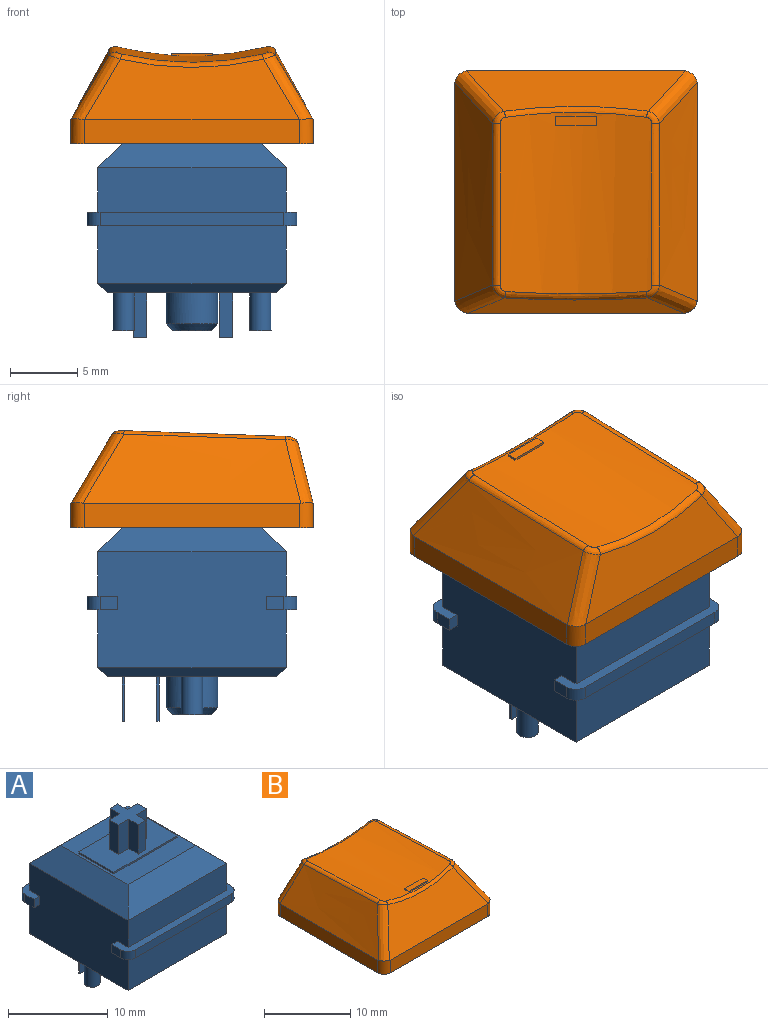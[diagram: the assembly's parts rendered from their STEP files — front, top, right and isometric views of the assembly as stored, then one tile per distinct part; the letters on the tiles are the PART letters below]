
ASSEMBLY  parts=2 mates=1
PART A: 69 faces, bbox 15.6x15.6x18.6 mm
  f0: plane 15.6x2.3mm, normal (0,0,-1), area 14.4mm2, adj f2,f3,f28,f30,f35,f60,f62,f63
  f1: plane 15.6x2.3mm, normal (0,0,-1), area 14.4mm2, adj f28,f30,f33,f34,f36,f59,f61,f64
  f2: plane 1.3x1mm, normal (1,0,0), area 1.3mm2, adj f0,f32,f62,f66
  f3: plane 1.3x1mm, normal (-1,0,0), area 1.3mm2, adj f0,f32,f63,f68
  f4: plane 15.6x2.3mm, normal (0,0,1), area 14.4mm2, adj f28,f30,f31,f33,f34,f36,f61,f64
  f5: plane 14x2.2mm, normal (-0.71,0,0.71), area 36.7mm2, adj f6,f7,f26,f30
  f6: plane 14x2.2mm, normal (0,-0.71,0.71), area 36.7mm2, adj f5,f7,f27,f31
  f7: plane 9.6x9.6mm, normal (0,0,1), area 47.2mm2, adj f5,f6,f8,f9,f10,f11,f26,f27
  f8: plane 5x0.2mm, normal (1,0,0), area 1mm2, adj f7,f9,f11,f12
  f9: plane 9x0.2mm, normal (0,1,0), area 1.8mm2, adj f7,f8,f10,f12
  f10: plane 5x0.2mm, normal (-1,0,0), area 1mm2, adj f7,f9,f11,f12
  f11: plane 9x0.2mm, normal (0,-1,0), area 1.8mm2, adj f7,f8,f10,f12
  f12: plane 9x5mm, normal (0,0,1), area 36.9mm2, adj f8,f9,f10,f11,f13,f14,f15,f16
  f13: plane 3.6x1.35mm, normal (1,0,0), area 4.9mm2, adj f12,f14,f24,f25
  f14: plane 3.6x1.08mm, normal (0,1,0), area 3.9mm2, adj f12,f13,f15,f25
  f15: plane 3.6x1.35mm, normal (-1,0,0), area 4.9mm2, adj f12,f14,f16,f25
  f16: plane 3.6x1.46mm, normal (0,1,0), area 5.3mm2, adj f12,f15,f17,f25
  f17: plane 3.6x1.3mm, normal (-1,0,0), area 4.7mm2, adj f12,f16,f18,f25
  f18: plane 3.6x1.46mm, normal (0,-1,0), area 5.3mm2, adj f12,f17,f19,f25
  f19: plane 3.6x1.35mm, normal (-1,0,0), area 4.9mm2, adj f12,f18,f20,f25
  f20: plane 3.6x1.08mm, normal (0,-1,0), area 3.9mm2, adj f12,f19,f21,f25
  f21: plane 3.6x1.35mm, normal (1,0,0), area 4.9mm2, adj f12,f20,f22,f25
  f22: plane 3.6x1.46mm, normal (0,-1,0), area 5.3mm2, adj f12,f21,f23,f25
  f23: plane 3.6x1.3mm, normal (1,0,0), area 4.7mm2, adj f12,f22,f24,f25
  f24: plane 3.6x1.46mm, normal (0,1,0), area 5.3mm2, adj f12,f13,f23,f25
  f25: plane 4x4mm, normal (0,0,1), area 8.1mm2, adj f13,f14,f15,f16,f17,f18,f19,f20
  f26: plane 14x2.2mm, normal (0,0.71,0.71), area 36.7mm2, adj f5,f7,f27,f29
  f27: plane 14x2.2mm, normal (0.71,0,0.71), area 36.7mm2, adj f6,f7,f26,f28
  f28: plane 14x8.6mm, normal (1,0,0), area 117.4mm2, adj f0,f1,f4,f27,f29,f31,f32,f55
  f29: plane 14x3.3mm, normal (0,1,0), area 46.2mm2, adj f26,f28,f30,f32
  f30: plane 14x8.6mm, normal (-1,0,0), area 117.4mm2, adj f0,f1,f4,f5,f29,f31,f32,f57
  f31: plane 14x3.3mm, normal (0,-1,0), area 46.2mm2, adj f4,f6,f28,f30
  f32: plane 15.6x2.3mm, normal (0,0,1), area 14.4mm2, adj f2,f3,f28,f29,f30,f35,f62,f63
  f33: plane 13.6x1mm, normal (0,-1,0), area 13.6mm2, adj f1,f4,f61,f64
  f34: plane 1.3x1mm, normal (1,0,0), area 1.3mm2, adj f1,f4,f61,f65
  f35: plane 13.6x1mm, normal (0,1,0), area 13.6mm2, adj f0,f32,f62,f63
  f36: plane 1.3x1mm, normal (-1,0,0), area 1.3mm2, adj f1,f4,f64,f67
  f37: plane 2.85x2.85mm, normal (0,0,-1), area 6.4mm2, adj f38
  f38: cone r=1.43mm half-angle=45deg, axis (0,0,1), area 7.4mm2, adj f37,f43
  f39: plane 1x0.2mm, normal (0,0,-1), area 0.2mm2, adj f44,f45,f46,f47
  f40: plane 1x0.2mm, normal (0,0,-1), area 0.2mm2, adj f48,f49,f50,f51
  f41: plane 1.6x1.6mm, normal (0,0,-1), area 2mm2, adj f52
  f42: plane 1.6x1.6mm, normal (0,0,-1), area 2mm2, adj f53
  f43: cylinder r=1.93mm len=3.85mm, axis (0,0,1), area 27.8mm2, adj f38,f54
  f44: plane 3.3x0.2mm, normal (-1,0,0), area 0.7mm2, adj f39,f45,f47,f54
  f45: plane 3.3x1mm, normal (0,1,0), area 3.3mm2, adj f39,f44,f46,f54
  f46: plane 3.3x0.2mm, normal (1,0,0), area 0.7mm2, adj f39,f45,f47,f54
  f47: plane 3.3x1mm, normal (0,-1,0), area 3.3mm2, adj f39,f44,f46,f54
  f48: plane 3.3x0.2mm, normal (-1,0,0), area 0.7mm2, adj f40,f49,f51,f54
  f49: plane 3.3x1mm, normal (0,1,0), area 3.3mm2, adj f40,f48,f50,f54
  f50: plane 3.3x0.2mm, normal (1,0,0), area 0.7mm2, adj f40,f49,f51,f54
  f51: plane 3.3x1mm, normal (0,-1,0), area 3.3mm2, adj f40,f48,f50,f54
  f52: cylinder r=0.8mm len=2.8mm, axis (0,0,1), area 14.1mm2, adj f41,f54
  f53: cylinder r=0.8mm len=2.8mm, axis (0,0,1), area 14.1mm2, adj f42,f54
  f54: plane 12.6x12.6mm, normal (0,0,-1), area 142.7mm2, adj f43,f44,f45,f46,f47,f48,f49,f50
  f55: plane 14x0.7mm, normal (0.71,0,-0.71), area 13.2mm2, adj f28,f54,f56,f58
  f56: plane 14x0.7mm, normal (0,0.71,-0.71), area 13.2mm2, adj f54,f55,f57,f60
  f57: plane 14x0.7mm, normal (-0.71,0,-0.71), area 13.2mm2, adj f30,f54,f56,f58
  f58: plane 14x0.7mm, normal (0,-0.71,-0.71), area 13.2mm2, adj f54,f55,f57,f59
  f59: plane 14x4.3mm, normal (0,-1,0), area 60.2mm2, adj f1,f28,f30,f58
  f60: plane 14x4.3mm, normal (0,1,0), area 60.2mm2, adj f0,f28,f30,f56
  f61: cylinder r=1mm len=1mm, axis (0,0,-1), area 1.6mm2, adj f1,f4,f33,f34
  f62: cylinder r=1mm len=1mm, axis (0,0,1), area 1.6mm2, adj f0,f2,f32,f35
  f63: cylinder r=1mm len=1mm, axis (0,0,-1), area 1.6mm2, adj f0,f3,f32,f35
  f64: cylinder r=1mm len=1mm, axis (0,0,1), area 1.6mm2, adj f1,f4,f33,f36
  f65: plane 1x0.8mm, normal (0,1,0), area 0.8mm2, adj f1,f4,f28,f34
  f66: plane 1x0.8mm, normal (0,-1,0), area 0.8mm2, adj f0,f2,f28,f32
  f67: plane 1x0.8mm, normal (0,1,0), area 0.8mm2, adj f1,f4,f30,f36
  f68: plane 1x0.8mm, normal (0,-1,0), area 0.8mm2, adj f0,f3,f30,f32
PART B: 55 faces, bbox 21.6x21x10.3 mm
  f0: cylinder r=22.9mm len=13.32mm, axis (0,1,-0.04), area 147.4mm2, adj f18,f19,f20,f21,f22,f23,f24,f25
  f1: plane 18x18mm, normal (0,0,-1), area 67.1mm2, adj f2,f3,f4,f5,f10,f12,f14,f16
  f2: plane 16x1.8mm, normal (1,0,0), area 28.8mm2, adj f1,f9,f10,f16
  f3: plane 16x1.8mm, normal (0,1,0), area 28.8mm2, adj f1,f6,f14,f15,f16,f17
  f4: plane 16x1.8mm, normal (-1,0,0), area 28.8mm2, adj f1,f7,f12,f14
  f5: plane 16x1.8mm, normal (0,-1,0), area 28.8mm2, adj f1,f8,f10,f12
  f6: plane 15.96x4.48mm, normal (0,0.97,0.24), area 56.8mm2, adj f3,f15,f17,f20
  f7: bspline ~18x5.51mm, area 80.2mm2, adj f4,f12,f13,f14,f15,f19
  f8: plane 16.27x5.09mm, normal (0,-0.86,0.51), area 74.6mm2, adj f5,f10,f11,f12,f13,f23
  f9: bspline ~18x5.51mm, area 80.2mm2, adj f2,f10,f11,f16,f17,f24
  f10: cylinder r=1mm len=1.89mm, axis (0,0,-1), area 2.9mm2, adj f1,f2,f5,f8,f9,f11
  f11: bspline ~6.77x4.7mm, area 8.7mm2, adj f8,f9,f10,f25
  f12: cylinder r=1mm len=1.89mm, axis (0,0,1), area 2.9mm2, adj f1,f4,f5,f7,f8,f13
  f13: bspline ~6.77x4.7mm, area 8.7mm2, adj f7,f8,f12,f21
  f14: cylinder r=1mm len=1.81mm, axis (0,0,-1), area 2.8mm2, adj f1,f3,f4,f7,f15
  f15: bspline ~8.13x5.44mm, area 7.9mm2, adj f3,f6,f7,f14,f18
  f16: cylinder r=1mm len=1.81mm, axis (0,0,1), area 2.8mm2, adj f1,f2,f3,f9,f17
  f17: bspline ~8.13x5.44mm, area 7.9mm2, adj f3,f6,f9,f16,f22
  f18: bspline ~1.19x1.01mm, area 0.7mm2, adj f0,f15,f19,f20
  f19: bspline ~16.72x0.91mm, area 7.8mm2, adj f0,f7,f18,f21
  f20: bspline ~10.66x0.99mm, area 6.9mm2, adj f0,f6,f18,f22
  f21: bspline ~1.2x1.09mm, area 0.6mm2, adj f0,f13,f19,f23
  f22: bspline ~1.17x1.02mm, area 0.7mm2, adj f0,f17,f20,f24
  f23: bspline ~10.72x0.84mm, area 5.8mm2, adj f0,f8,f21,f25
  f24: bspline ~16.72x0.91mm, area 7.8mm2, adj f0,f9,f22,f25
  f25: bspline ~1.2x1.09mm, area 0.6mm2, adj f0,f11,f23,f24
  f26: plane 16.02x1.56mm, normal (-1,0,0), area 24.6mm2, adj f1,f27,f29,f33
  f27: plane 16x1.68mm, normal (0,-1,0), area 26.8mm2, adj f1,f26,f28,f30,f31,f33
  f28: plane 16.02x1.56mm, normal (1,0,0), area 24.6mm2, adj f1,f27,f29,f31
  f29: plane 16.02x1.54mm, normal (0,1,0), area 24.4mm2, adj f1,f26,f28,f32
  f30: plane 16.19x4.4mm, normal (0,-0.97,-0.24), area 50.7mm2, adj f27,f31,f33,f34
  f31: offset ~20x7.51mm, area 71.4mm2, adj f27,f28,f30,f32,f34
  f32: plane 16.71x5.3mm, normal (0,0.86,-0.51), area 66.9mm2, adj f29,f31,f33,f34
  f33: offset ~20x7.51mm, area 71.4mm2, adj f26,f27,f30,f32,f34
  f34: cylinder r=23.9mm len=12.29mm, axis (0,1,-0.04), area 112.6mm2, adj f30,f31,f32,f33,f46
  f35: plane 4.69x1.5mm, normal (-1,0,0), area 7mm2, adj f36,f44,f45,f49
  f36: plane 4.78x1.5mm, normal (0,-1,0), area 7.1mm2, adj f35,f37,f45,f49
  f37: plane 4.82x1.3mm, normal (-1,0,0), area 6.2mm2, adj f36,f38,f45,f49
  f38: plane 4.82x1.5mm, normal (0,1,0), area 7.2mm2, adj f37,f39,f45,f49
  f39: plane 4.79x1.5mm, normal (-1,0,0), area 7.1mm2, adj f38,f40,f45,f49
  f40: plane 4.79x1.3mm, normal (0,1,0), area 6.2mm2, adj f39,f41,f45,f49
  f41: plane 4.79x1.5mm, normal (1,0,0), area 7.1mm2, adj f40,f42,f45,f49
  f42: plane 4.82x1.5mm, normal (0,1,0), area 7.2mm2, adj f41,f43,f45,f49
  f43: plane 4.82x1.3mm, normal (1,0,0), area 6.2mm2, adj f42,f45,f47,f49
  f44: plane 4.64x1.3mm, normal (0,-1,0), area 6mm2, adj f35,f45,f48,f49
  f45: plane 5.5x5.5mm, normal (0,0,-1), area 14.3mm2, adj f35,f36,f37,f38,f39,f40,f41,f42
  f46: cylinder r=2.75mm len=5.5mm, axis (0,0,-1), area 84mm2, adj f34,f45
  f47: plane 4.78x1.5mm, normal (0,-1,0), area 7.1mm2, adj f43,f45,f48,f49
  f48: plane 4.69x1.5mm, normal (1,0,0), area 7mm2, adj f44,f45,f47,f49
  f49: cylinder r=23.9mm len=4.3mm, axis (0,1,-0.04), area 9.5mm2, adj f35,f36,f37,f38,f39,f40,f41,f42
  f50: plane 0.71x0.18mm, normal (1,0,0), area 0.1mm2, adj f0,f51,f53,f54
  f51: plane 3x0.2mm, normal (0,1,-0.04), area 0.6mm2, adj f0,f50,f52,f54
  f52: plane 0.71x0.18mm, normal (-1,0,0), area 0.1mm2, adj f0,f51,f53,f54
  f53: plane 3x0.2mm, normal (0,-1,0.04), area 0.6mm2, adj f0,f50,f52,f54
  f54: plane 3x0.7mm, normal (0,0.04,1), area 2.1mm2, adj f50,f51,f52,f53
PLACE A at identity fixed
PLACE B rot(axis=(0,0,1),180deg) t=(0,0,11.1)mm
MATE fastened B.f46 <-> A.f38  axis (0,0,-1) through (0,0,11.7)mm
